# Revit family: Kohler Pitch K-74039IN-4FP-CP Family
name_source: partatom
category: Plumbing Fixtures
units: mm (PartAtom-declared; Revit-internal decimal feet)

## family parameters
Always vertical = Yes
Cut with Voids When Loaded = No
Part Type = Normal
Room Calculation Point = No
Round Connector Dimension = Use Diameter
Shared = No
Work Plane-Based = Yes

## types (1)
- Kohler Pitch K-74039IN-4FP-CP
    Default Elevation = 1219 mm
    Disclaimer = Although care has been taken to ensure, to the best of our knowledge, that all data and information contained herein is accurate to the extent that it relates to either matters of fact or accepted practice at the time of issue. MDFC (Pty) Ltd assumes no responsibility for any errors in, or misinterpretation of, such data and/ or information or any loss or damage arising from, or related to its use.
    Height = 160 mm
    Manufacturer = Kohler Co.
    Material = Chrome
    Model = Kohler Pitch K-74039IN-4FP-CP
    Telephone = 011 050 9000
    Thickness = 71 mm  [stored 0.23294 ft]
    URL = www.africa.kohler.com
    Width = 110 mm

note: [stored X ft] marks values corroborated as IEEE doubles in the binary element streams (Revit-internal decimal feet)

## geometry (parser evidence)
native form markers: Sweep x3
no freeform markers — native parametric forms only
